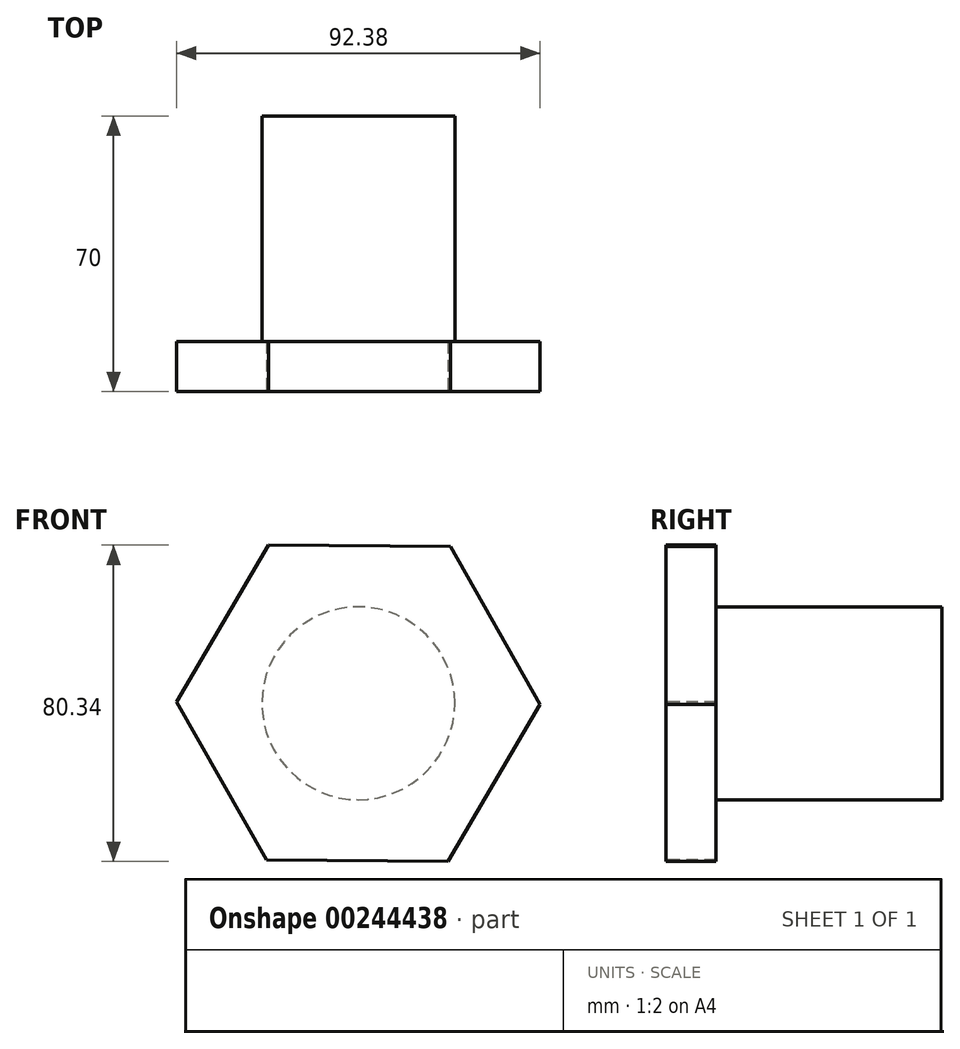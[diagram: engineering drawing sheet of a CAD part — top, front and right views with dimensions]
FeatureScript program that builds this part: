
annotation { "Feature Type Name" : "Feature", "Feature Type Description" : "" }
export const myFeature = defineFeature(function(context is Context, id is Id, definition is map)
    precondition{}
    {
        {
            var Q0;
            Q0=qCreatedBy(makeId("Front.planeOp"),FACE);
            var sketch = newSketch(context, id + "F0", { "sketchPlane" : qUnion([Q0])});
            skCircle(sketch, "E0", {"center": v(0, 0) * mm, "radius": 24.5 * mm});
            skSolve(sketch);
        }
        {
            var Q0;
            Q0=makeQuery(id+"F0.imprint","IMPRINT",FACE,{"disambiguationData":[TD([[makeQuery(id+"F0.imprint","IMPRINT",EDGE,{"derivedFrom":sQuery(id+"F0.wireOp",EDGE,"E0")}),1.0]])]});
            extrude(context, id + "F1", {"entities" : qUnion([Q0]), "depth" : 70 * mm});
        }
        {
            var Q0;
            Q0=makeQuery(id+"F1.opExtrude","CAP_FACE",FACE,{"disambiguationData":[OSD([sQuery(id+"F0.wireOp",EDGE,"E0")])],"isStart":false});
            var sketch = newSketch(context, id + "F2", { "sketchPlane" : qUnion([Q0])});
            skCircle(sketch, "E1.cCircle", {"center": v(0, 0) * mm, "radius": 40 * mm, "construction": true});
            skLineSegment(sketch, "E1.0", {"start": v(23.39, 39.83) * mm, "end": v(46.19, -0.34) * mm});
            skLineSegment(sketch, "E1.1", {"start": v(46.19, -0.34) * mm, "end": v(22.8, -40.17) * mm});
            skLineSegment(sketch, "E1.2", {"start": v(22.8, -40.17) * mm, "end": v(-23.39, -39.83) * mm});
            skLineSegment(sketch, "E1.3", {"start": v(-23.39, -39.83) * mm, "end": v(-46.19, 0.34) * mm});
            skLineSegment(sketch, "E1.4", {"start": v(-46.19, 0.34) * mm, "end": v(-22.8, 40.17) * mm});
            skLineSegment(sketch, "E1.5", {"start": v(-22.8, 40.17) * mm, "end": v(23.39, 39.83) * mm});
            skPoint(sketch, "E1.0.midPoint", {"position": v(34.79, 19.75) * mm});
            skSolve(sketch);
        }
        {
            var Q0;
            Q0=makeQuery(id+"F2.imprint","IMPRINT",FACE,{"disambiguationData":[TD([[makeQuery(id+"F2.imprint","IMPRINT",EDGE,{"derivedFrom":sQuery(id+"F2.wireOp",EDGE,"E1.0")}),-1.0]])]});
            extrude(context, id + "F3", {"entities" : qUnion([Q0]), "operationType" : NewBodyOperationType.ADD, "oppositeDirection" : true, "depth" : 12.7 * mm});
        }
    });
